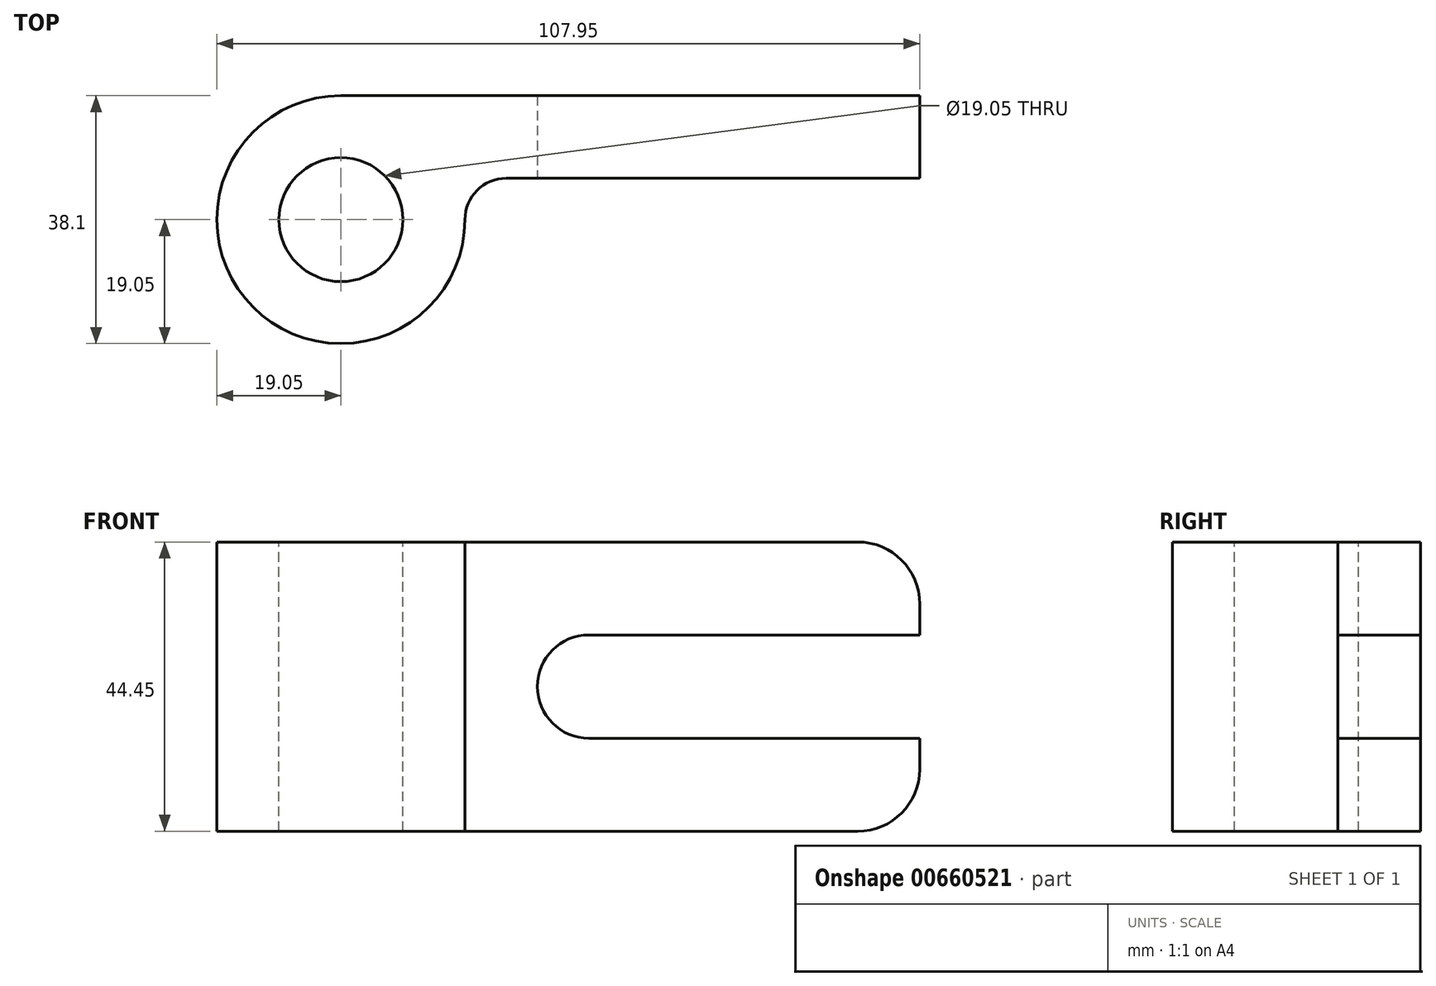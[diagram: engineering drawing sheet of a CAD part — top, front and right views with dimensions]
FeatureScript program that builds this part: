
annotation { "Feature Type Name" : "Feature", "Feature Type Description" : "" }
export const myFeature = defineFeature(function(context is Context, id is Id, definition is map)
    precondition{}
    {
        {
            var Q0;
            Q0=qCreatedBy(makeId("Top.planeOp"),FACE);
            var sketch = newSketch(context, id + "F0", { "sketchPlane" : qUnion([Q0])});
            skCircle(sketch, "E0", {"center": v(0, 0) * mm, "radius": 9.53 * mm});
            skArc(sketch, "E1", {"start": v(0, 19.05) * mm, "mid": v(-13.47, -13.47) * mm, "end": v(19.05, 0) * mm});
            skLineSegment(sketch, "E2", {"start": v(0, 19.05) * mm, "end": v(38.1, 19.05) * mm});
            skLineSegment(sketch, "E3", {"start": v(38.1, 19.05) * mm, "end": v(88.9, 19.05) * mm});
            skLineSegment(sketch, "E4", {"start": v(88.9, 19.05) * mm, "end": v(88.9, 6.35) * mm});
            skLineSegment(sketch, "E5", {"start": v(88.9, 6.35) * mm, "end": v(25.4, 6.35) * mm});
            skArc(sketch, "E6", {"start": v(25.4, 6.35) * mm, "mid": v(20.9, 4.5) * mm, "end": v(19.05, 0) * mm});
            skSolve(sketch);
        }
        {
            var Q0;
            Q0=makeQuery(id+"F0.imprint","IMPRINT",FACE,{"disambiguationData":[TD([[makeQuery(id+"F0.imprint","IMPRINT",EDGE,{"derivedFrom":sQuery(id+"F0.wireOp",EDGE,"E0")}),-1.0]])]});
            extrude(context, id + "F1", {"entities" : qUnion([Q0]), "oppositeDirection" : true, "depth" : 44.45 * mm, "offsetDistance" : 25.4 * mm});
        }
        {
            var Q0;
            Q0=makeQuery(id+"F1.opExtrude","SWEPT_FACE",FACE,{"disambiguationData":[OSD([sQuery(id+"F0.wireOp",EDGE,"E5")])]});
            var sketch = newSketch(context, id + "F2", { "sketchPlane" : qUnion([Q0])});
            skLineSegment(sketch, "E7", {"start": v(88.9, -30.16) * mm, "end": v(38.1, -30.16) * mm});
            skLineSegment(sketch, "E8", {"start": v(38.1, -14.29) * mm, "end": v(88.9, -14.29) * mm});
            skLineSegment(sketch, "E9", {"start": v(88.9, 0) * mm, "end": v(88.9, -22.23) * mm});
            skArc(sketch, "E10", {"start": v(38.1, -14.29) * mm, "mid": v(30.16, -22.23) * mm, "end": v(38.1, -30.16) * mm});
            skLineSegment(sketch, "E11", {"start": v(88.9, -30.16) * mm, "end": v(88.9, -37.31) * mm});
            skArc(sketch, "E12", {"start": v(79.38, -44.45) * mm, "mid": v(86.11, -41.66) * mm, "end": v(88.9, -34.93) * mm});
            skLineSegment(sketch, "E13", {"start": v(79.38, -44.45) * mm, "end": v(88.9, -44.45) * mm});
            skLineSegment(sketch, "E14", {"start": v(88.9, -44.45) * mm, "end": v(88.9, -34.93) * mm});
            skArc(sketch, "E15", {"start": v(88.9, -9.53) * mm, "mid": v(86.11, -2.79) * mm, "end": v(79.38, 0) * mm});
            skLineSegment(sketch, "E16", {"start": v(79.38, 0) * mm, "end": v(88.9, 0) * mm});
            skSolve(sketch);
        }
        {
            var Q0;
            {var subQ2=sQuery(id+"F2.wireOp",EDGE,"E15");Q0=makeQuery(id+"F2.imprint","IMPRINT",FACE,{"disambiguationData":[TD([[makeQuery(id+"F2.imprint","IMPRINT",EDGE,{"derivedFrom":subQ2}),-1.0]])]});}
            var Q1;
            {var subQ4=sQuery(id+"F2.wireOp",EDGE,"E7");Q1=makeQuery(id+"F2.imprint","IMPRINT",FACE,{"disambiguationData":[TD([[makeQuery(id+"F2.imprint","IMPRINT",EDGE,{"derivedFrom":subQ4}),-1.0]])]});}
            var Q2;
            {var subQ0=sQuery(id+"F2.wireOp",EDGE,"E12");Q2=makeQuery(id+"F2.imprint","IMPRINT",FACE,{"disambiguationData":[TD([[makeQuery(id+"F2.imprint","IMPRINT",EDGE,{"derivedFrom":subQ0}),-1.0]])]});}
            extrude(context, id + "F3", {"entities" : qUnion([Q0, Q1, Q2]), "operationType" : NewBodyOperationType.REMOVE, "oppositeDirection" : true, "depth" : 12.7 * mm, "offsetDistance" : 25.4 * mm});
        }
    });
